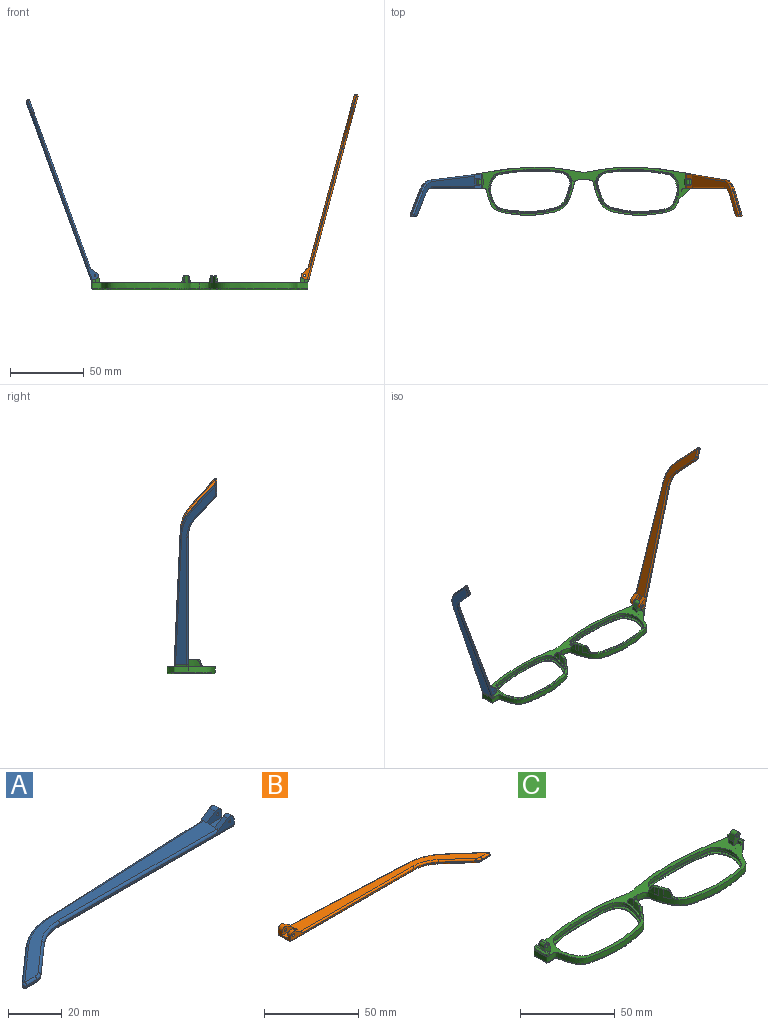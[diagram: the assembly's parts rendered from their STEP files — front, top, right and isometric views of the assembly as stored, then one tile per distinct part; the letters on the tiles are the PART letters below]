
ASSEMBLY  parts=3 mates=2
PART A: 43 faces, bbox 130.2x29.5x5.9 mm
  f0: plane 9.62x3.72mm, normal (1,0,0), area 24.7mm2, adj f1,f3,f4,f5,f10,f16,f18,f28
  f1: cylinder r=2.2mm len=3.45mm, axis (0,-1,0), area 11mm2, adj f0,f2,f4,f37
  f2: plane 6.01x3.91mm, normal (-0.55,0,0.84), area 12.7mm2, adj f1,f4,f9,f19,f37
  f3: plane 2.26x0.1mm, normal (0,0,1), area 0.1mm2, adj f0,f5,f18
  f4: plane 92.1x4.9mm, normal (0,-1,0), area 79.9mm2, adj f0,f1,f2,f14,f19,f36,f42
  f5: plane 93.42x4.13mm, normal (-0.04,1,0), area 64.8mm2, adj f0,f3,f11,f15,f17,f27,f28
  f6: plane 17.82x15.72mm, normal (-0.66,0.75,0), area 14.3mm2, adj f11,f12,f25,f30
  f7: plane 5.46x0.6mm, normal (0,-1,0), area 3.3mm2, adj f12,f13,f23,f32
  f8: plane 14.99x13.23mm, normal (0.66,-0.75,0), area 12mm2, adj f13,f14,f21,f34
  f9: plane 121.18x26.73mm, normal (0,0,1), area 627.7mm2, adj f2,f17,f19,f20,f21,f22,f23,f25
  f10: plane 129.1x27.08mm, normal (0,0,-1), area 686.5mm2, adj f0,f28,f29,f30,f32,f33,f34,f35
  f11: cylinder r=30mm len=18.52mm, axis (0,0,-1), area 12.2mm2, adj f5,f6,f26,f29
  f12: cylinder r=1mm len=1.75mm, axis (0,0,-1), area 1.5mm2, adj f6,f7,f24,f31
  f13: cylinder r=5mm len=3.31mm, axis (0,0,-1), area 2.2mm2, adj f7,f8,f22,f33
  f14: cylinder r=20mm len=13.23mm, axis (0,0,1), area 8.7mm2, adj f4,f8,f20,f35
  f15: plane 5.66x0.25mm, normal (0,0,-1), area 0.7mm2, adj f5,f17,f18
  f16: cylinder r=2.2mm len=3.45mm, axis (0,-1,0), area 14.8mm2, adj f0,f17,f18,f38
  f17: plane 6.01x3.91mm, normal (-0.55,0,0.84), area 16.9mm2, adj f5,f9,f15,f16,f18,f27,f38
  f18: plane 7.92x3.3mm, normal (0,1,0), area 15.9mm2, adj f0,f3,f15,f16,f17,f41
  f19: cylinder r=1mm len=84.18mm, axis (-1,0,0), area 131.4mm2, adj f2,f4,f9,f20
  f20: torus R=21mm, axis (0,0,1), area 23.1mm2, adj f9,f14,f19,f21
  f21: cylinder r=1mm len=15.65mm, axis (-0.75,-0.66,0), area 31.4mm2, adj f8,f9,f20,f22
  f22: torus R=4mm, axis (0,0,1), area 5.3mm2, adj f9,f13,f21,f23
  f23: cylinder r=1mm len=5.46mm, axis (-1,0,0), area 8.6mm2, adj f7,f9,f22,f24
  f24: sphere r=1mm, area 2.4mm2, adj f12,f23,f25
  f25: cylinder r=1mm len=18.48mm, axis (0.75,0.66,0), area 37.3mm2, adj f6,f9,f24,f26
  f26: torus R=29mm, axis (0,0,1), area 31.6mm2, adj f9,f11,f25,f27
  f27: cylinder r=1mm len=85.5mm, axis (1,0.04,0), area 133.5mm2, adj f5,f9,f17,f26
  f28: cylinder r=1mm len=93.46mm, axis (-1,-0.04,0), area 146.9mm2, adj f0,f5,f10,f29
  f29: torus R=29mm, axis (0,0,1), area 31.6mm2, adj f10,f11,f28,f30
  f30: cylinder r=1mm len=18.48mm, axis (-0.75,-0.66,0), area 37.3mm2, adj f6,f10,f29,f31
  f31: sphere r=1mm, area 2.4mm2, adj f12,f30,f32
  f32: cylinder r=1mm len=5.46mm, axis (1,0,0), area 8.6mm2, adj f7,f10,f31,f33
  f33: torus R=4mm, axis (0,0,1), area 5.3mm2, adj f10,f13,f32,f34
  f34: cylinder r=1mm len=15.65mm, axis (0.75,0.66,0), area 31.4mm2, adj f8,f10,f33,f35
  f35: torus R=21mm, axis (0,0,1), area 23.1mm2, adj f10,f14,f34,f36
  f36: cylinder r=1mm len=92.1mm, axis (1,0,0), area 144.7mm2, adj f0,f4,f10,f35
  f37: plane 7.92x4.7mm, normal (0,1,0), area 27mm2, adj f0,f1,f2,f39,f40,f42
  f38: plane 7.92x4.7mm, normal (0,-1,0), area 27mm2, adj f0,f16,f17,f39,f40,f41
  f39: plane 7.92x4.1mm, normal (0,0,1), area 32.5mm2, adj f0,f37,f38,f40
  f40: plane 4.1x1.4mm, normal (1,0,0), area 5.7mm2, adj f9,f37,f38,f39
  f41: cylinder r=0.5mm len=3.1mm, axis (0,-1,0), area 9.7mm2, adj f18,f38
  f42: cylinder r=0.5mm len=2.3mm, axis (0,-1,0), area 7.2mm2, adj f4,f37
PART B: 43 faces, bbox 130.2x29.5x5.9 mm
  f0: plane 9.62x3.72mm, normal (-1,0,0), area 24.7mm2, adj f1,f3,f4,f5,f10,f16,f18,f28
  f1: cylinder r=2.2mm len=3.45mm, axis (0,-1,0), area 11mm2, adj f0,f2,f4,f37
  f2: plane 6.01x3.91mm, normal (0.55,0,0.84), area 12.7mm2, adj f1,f4,f9,f19,f37
  f3: plane 2.26x0.1mm, normal (0,0,1), area 0.1mm2, adj f0,f5,f18
  f4: plane 92.1x4.9mm, normal (0,-1,0), area 78.2mm2, adj f0,f1,f2,f14,f19,f36,f42
  f5: plane 93.42x4.13mm, normal (0.04,1,0), area 64.8mm2, adj f0,f3,f11,f15,f17,f27,f28
  f6: plane 17.82x15.72mm, normal (0.66,0.75,0), area 14.3mm2, adj f11,f12,f25,f30
  f7: plane 5.46x0.6mm, normal (0,-1,0), area 3.3mm2, adj f12,f13,f23,f32
  f8: plane 14.99x13.23mm, normal (-0.66,-0.75,0), area 12mm2, adj f13,f14,f21,f34
  f9: plane 121.18x26.73mm, normal (0,0,1), area 627.7mm2, adj f2,f17,f19,f20,f21,f22,f23,f25
  f10: plane 129.1x27.08mm, normal (0,0,-1), area 686.5mm2, adj f0,f28,f29,f30,f32,f33,f34,f35
  f11: cylinder r=30mm len=18.52mm, axis (0,0,-1), area 12.2mm2, adj f5,f6,f26,f29
  f12: cylinder r=1mm len=1.75mm, axis (0,0,-1), area 1.5mm2, adj f6,f7,f24,f31
  f13: cylinder r=5mm len=3.31mm, axis (0,0,-1), area 2.2mm2, adj f7,f8,f22,f33
  f14: cylinder r=20mm len=13.23mm, axis (0,0,1), area 8.7mm2, adj f4,f8,f20,f35
  f15: plane 5.66x0.25mm, normal (0,0,-1), area 0.7mm2, adj f5,f17,f18
  f16: cylinder r=2.2mm len=3.45mm, axis (0,-1,0), area 14.8mm2, adj f0,f17,f18,f38
  f17: plane 6.01x3.91mm, normal (0.55,0,0.84), area 16.9mm2, adj f5,f9,f15,f16,f18,f27,f38
  f18: plane 7.92x3.3mm, normal (0,1,0), area 14.3mm2, adj f0,f3,f15,f16,f17,f41
  f19: cylinder r=1mm len=84.18mm, axis (1,0,0), area 131.4mm2, adj f2,f4,f9,f20
  f20: torus R=21mm, axis (0,0,1), area 23.1mm2, adj f9,f14,f19,f21
  f21: cylinder r=1mm len=15.65mm, axis (0.75,-0.66,0), area 31.4mm2, adj f8,f9,f20,f22
  f22: torus R=4mm, axis (0,0,1), area 5.3mm2, adj f9,f13,f21,f23
  f23: cylinder r=1mm len=5.46mm, axis (1,0,0), area 8.6mm2, adj f7,f9,f22,f24
  f24: sphere r=1mm, area 2.4mm2, adj f12,f23,f25
  f25: cylinder r=1mm len=18.48mm, axis (-0.75,0.66,0), area 37.3mm2, adj f6,f9,f24,f26
  f26: torus R=29mm, axis (0,0,1), area 31.6mm2, adj f9,f11,f25,f27
  f27: cylinder r=1mm len=85.5mm, axis (-1,0.04,0), area 133.5mm2, adj f5,f9,f17,f26
  f28: cylinder r=1mm len=93.46mm, axis (1,-0.04,0), area 146.9mm2, adj f0,f5,f10,f29
  f29: torus R=29mm, axis (0,0,1), area 31.6mm2, adj f10,f11,f28,f30
  f30: cylinder r=1mm len=18.48mm, axis (0.75,-0.66,0), area 37.3mm2, adj f6,f10,f29,f31
  f31: sphere r=1mm, area 2.4mm2, adj f12,f30,f32
  f32: cylinder r=1mm len=5.46mm, axis (-1,0,0), area 8.6mm2, adj f7,f10,f31,f33
  f33: torus R=4mm, axis (0,0,1), area 5.3mm2, adj f10,f13,f32,f34
  f34: cylinder r=1mm len=15.65mm, axis (-0.75,0.66,0), area 31.4mm2, adj f8,f10,f33,f35
  f35: torus R=21mm, axis (0,0,1), area 23.1mm2, adj f10,f14,f34,f36
  f36: cylinder r=1mm len=92.1mm, axis (-1,0,0), area 144.7mm2, adj f0,f4,f10,f35
  f37: plane 7.92x4.7mm, normal (0,1,0), area 25.4mm2, adj f0,f1,f2,f39,f40,f42
  f38: plane 7.92x4.7mm, normal (0,-1,0), area 25.4mm2, adj f0,f16,f17,f39,f40,f41
  f39: plane 7.92x4.1mm, normal (0,0,1), area 32.5mm2, adj f0,f37,f38,f40
  f40: plane 4.1x1.4mm, normal (-1,0,0), area 5.7mm2, adj f9,f37,f38,f39
  f41: cylinder r=0.88mm len=3.1mm, axis (0,-1,0), area 17mm2, adj f18,f38
  f42: cylinder r=0.88mm len=2.3mm, axis (0,-1,0), area 12.6mm2, adj f4,f37
PART C: 88 faces, bbox 148.2x33.5x17.9 mm
  f0: extruded ~10.56x5mm, area 41.6mm2, adj f2,f37,f38,f40,f43
  f1: extruded ~5.01x5mm, area 12.8mm2, adj f2,f37,f39
  f2: plane 147.77x33.33mm, normal (0,0,1), area 824.9mm2, adj f0,f1,f4,f5,f6,f7,f8,f21
  f3: plane 3.96x1.78mm, normal (0,0,1), area 0mm2, adj f7,f36
  f4: plane 1.2x0.04mm, normal (0,0,1), area 0mm2, adj f2,f7,f22
  f5: plane 6.91x4.89mm, normal (0,1,0), area 21mm2, adj f2,f21,f25,f27,f28,f29,f30,f31
  f6: plane 6.91x4.89mm, normal (0,-1,0), area 21mm2, adj f2,f21,f26,f27,f28,f29,f30,f31
  f7: extruded ~73.32x32.67mm, area 509.4mm2, adj f2,f3,f4,f8,f13,f14,f15,f16
  f8: extruded ~33.86x3.5mm, area 119.4mm2, adj f2,f7,f19,f52
  f9: plane 144.79x30.69mm, normal (0,0,-1), area 451.5mm2, adj f14,f16,f18,f19,f20,f57,f59,f61
  f10: plane 56.61x30.2mm, normal (0,0,1), area 187.1mm2, adj f11,f20
  f11: extruded ~56.31x30.04mm, area 148mm2, adj f10,f12
  f12: extruded ~56.31x30.04mm, area 296.1mm2, adj f11,f41,f42
  f13: plane 2.59x0.69mm, normal (0,0,1), area 0mm2, adj f7,f35
  f14: bspline ~73.03x25.58mm, area 149.9mm2, adj f7,f9,f15,f57
  f15: bspline ~1x1mm, area 0.8mm2, adj f7,f14,f16
  f16: bspline ~8.66x1.21mm, area 12.7mm2, adj f7,f9,f15,f17
  f17: bspline ~1.04x1mm, area 0.8mm2, adj f7,f16,f18
  f18: bspline ~45.4x5.77mm, area 61.6mm2, adj f7,f9,f17,f19
  f19: bspline ~36.19x4.34mm, area 53.5mm2, adj f8,f9,f18,f62
  f20: bspline ~55.75x29.24mm, area 220mm2, adj f9,f10
  f21: plane 3.8x2.3mm, normal (-1,0,0), area 8.7mm2, adj f2,f5,f6,f28
  f22: plane 2.79x2.56mm, normal (0,-1,0), area 3.9mm2, adj f4,f26,f27,f33,f44
  f23: plane 7.68x1.6mm, normal (0.94,0,-0.34), area 13.1mm2, adj f2,f33,f34,f44
  f24: plane 2.1x1.69mm, normal (0,1,0), area 2.8mm2, adj f2,f25,f27,f34,f44
  f25: plane 3.41x2.1mm, normal (-1,0,0), area 7.2mm2, adj f2,f5,f24,f27
  f26: plane 2.46x2.1mm, normal (-1,0,0), area 5.2mm2, adj f2,f6,f22,f27
  f27: plane 9.67x1.25mm, normal (0,0,1), area 8.8mm2, adj f5,f6,f22,f24,f25,f26,f29,f44
  f28: plane 3.8x3.31mm, normal (-0.94,0,0.34), area 13.4mm2, adj f5,f6,f21,f31
  f29: plane 3.8x2.21mm, normal (0.94,0,-0.34), area 8.9mm2, adj f5,f6,f27,f30
  f30: cylinder r=1.98mm len=3.8mm, axis (0,-1,0), area 11.5mm2, adj f5,f6,f29,f31
  f31: cylinder r=1.98mm len=3.8mm, axis (0,1,0), area 11.5mm2, adj f5,f6,f28,f30
  f32: cylinder r=0.95mm len=3.8mm, axis (0,-1,0), area 22.7mm2, adj f5,f6
  f33: cone r=1mm half-angle=20deg, axis (0,0,1), area 2.3mm2, adj f2,f22,f23,f44
  f34: cylinder r=1mm len=2.28mm, axis (-0.34,0,-0.94), area 3mm2, adj f2,f23,f24,f44
  f35: extruded ~5x2.58mm, area 12.9mm2, adj f7,f13,f38,f39
  f36: extruded ~5x3.93mm, area 20.5mm2, adj f3,f7,f38,f40,f43
  f37: extruded ~5x0.31mm, area 1.6mm2, adj f0,f1,f2,f38
  f38: plane 7.62x2.87mm, normal (0,0,1), area 8.6mm2, adj f0,f7,f35,f36,f37,f39,f40
  f39: bspline ~15.49x15.48mm, area 16.3mm2, adj f1,f2,f7,f35,f38
  f40: bspline ~7.28x7.28mm, area 5.6mm2, adj f0,f36,f38,f43
  f41: plane 56.54x30.13mm, normal (0,0,-1), area 51.5mm2, adj f12,f42
  f42: bspline ~55.69x29.23mm, area 101.4mm2, adj f2,f12,f41
  f43: bspline ~3.67x3.45mm, area 5.2mm2, adj f0,f2,f7,f36,f40
  f44: plane 9.73x1.44mm, normal (0.34,0,0.94), area 13.9mm2, adj f22,f23,f24,f27,f33,f34
  f45: extruded ~10.56x5mm, area 41.6mm2, adj f2,f80,f81,f83,f86
  f46: extruded ~5.01x5mm, area 12.8mm2, adj f2,f80,f82
  f47: plane 3.96x1.78mm, normal (0,0,1), area 0mm2, adj f51,f79
  f48: plane 1.2x0.04mm, normal (0,0,1), area 0mm2, adj f2,f51,f65
  f49: plane 6.91x4.89mm, normal (0,1,0), area 21mm2, adj f2,f64,f68,f70,f71,f72,f73,f74
  f50: plane 6.91x4.89mm, normal (0,-1,0), area 21mm2, adj f2,f64,f69,f70,f71,f72,f73,f74
  f51: extruded ~73.32x32.67mm, area 509.4mm2, adj f2,f7,f47,f48,f52,f56,f57,f58
  f52: extruded ~33.86x3.5mm, area 119.4mm2, adj f2,f8,f51,f62
  f53: plane 56.61x30.2mm, normal (0,0,1), area 187.1mm2, adj f54,f63
  f54: extruded ~56.31x30.04mm, area 148mm2, adj f53,f55
  f55: extruded ~56.31x30.04mm, area 296.1mm2, adj f54,f84,f85
  f56: plane 2.59x0.69mm, normal (0,0,1), area 0mm2, adj f51,f78
  f57: bspline ~73.03x25.58mm, area 150mm2, adj f9,f14,f51,f58
  f58: bspline ~1x1mm, area 0.8mm2, adj f51,f57,f59
  f59: bspline ~8.66x1.21mm, area 12.7mm2, adj f9,f51,f58,f60
  f60: bspline ~1.04x1mm, area 0.7mm2, adj f51,f59,f61
  f61: bspline ~45.4x5.77mm, area 61.6mm2, adj f9,f51,f60,f62
  f62: bspline ~36.19x4.34mm, area 53.5mm2, adj f9,f19,f52,f61
  f63: bspline ~55.75x29.24mm, area 220mm2, adj f9,f53
  f64: plane 3.8x2.3mm, normal (1,0,0), area 8.7mm2, adj f2,f49,f50,f71
  f65: plane 2.79x2.56mm, normal (0,-1,0), area 3.9mm2, adj f48,f69,f70,f76,f87
  f66: plane 7.68x1.6mm, normal (-0.94,0,-0.34), area 13.1mm2, adj f2,f76,f77,f87
  f67: plane 2.1x1.69mm, normal (0,1,0), area 2.8mm2, adj f2,f68,f70,f77,f87
  f68: plane 3.41x2.1mm, normal (1,0,0), area 7.2mm2, adj f2,f49,f67,f70
  f69: plane 2.46x2.1mm, normal (1,0,0), area 5.2mm2, adj f2,f50,f65,f70
  f70: plane 9.67x1.25mm, normal (0,0,1), area 8.8mm2, adj f49,f50,f65,f67,f68,f69,f72,f87
  f71: plane 3.8x3.31mm, normal (0.94,0,0.34), area 13.4mm2, adj f49,f50,f64,f74
  f72: plane 3.8x2.21mm, normal (-0.94,0,-0.34), area 8.9mm2, adj f49,f50,f70,f73
  f73: cylinder r=1.98mm len=3.8mm, axis (0,-1,0), area 11.5mm2, adj f49,f50,f72,f74
  f74: cylinder r=1.98mm len=3.8mm, axis (0,1,0), area 11.5mm2, adj f49,f50,f71,f73
  f75: cylinder r=0.95mm len=3.8mm, axis (0,-1,0), area 22.7mm2, adj f49,f50
  f76: cone r=1mm half-angle=20deg, axis (0,0,1), area 2.3mm2, adj f2,f65,f66,f87
  f77: cylinder r=1mm len=2.28mm, axis (0.34,0,-0.94), area 3mm2, adj f2,f66,f67,f87
  f78: extruded ~5x2.58mm, area 12.9mm2, adj f51,f56,f81,f82
  f79: extruded ~5x3.93mm, area 20.5mm2, adj f47,f51,f81,f83,f86
  f80: extruded ~5x0.31mm, area 1.6mm2, adj f2,f45,f46,f81
  f81: plane 7.62x2.87mm, normal (0,0,1), area 8.6mm2, adj f45,f51,f78,f79,f80,f82,f83
  f82: bspline ~15.49x15.48mm, area 16.3mm2, adj f2,f46,f51,f78,f81
  f83: bspline ~7.28x7.28mm, area 5.6mm2, adj f45,f79,f81,f86
  f84: plane 56.54x30.13mm, normal (0,0,-1), area 51.5mm2, adj f55,f85
  f85: bspline ~55.69x29.23mm, area 101.4mm2, adj f2,f55,f84
  f86: bspline ~3.67x3.45mm, area 5.2mm2, adj f2,f45,f51,f79,f83
  f87: plane 9.73x1.44mm, normal (-0.34,0,0.94), area 13.9mm2, adj f65,f66,f67,f70,f76,f77
PLACE A rot(axis=(0,1,0),70deg) t=(-164.62,-11.41,86.54)mm
PLACE B rot(axis=(0,-1,0),75deg) t=(-11.67,-11.41,-31.01)mm
PLACE C t=(-69.62,-6.9,23.33)mm
MATE revolute A.f1 <-> C.f74  axis (0,-1,0) through (-140.74,-2.95,31.75)mm
MATE revolute B.f41 <-> C.f30  axis (0,-1,0) through (1.34,-2.95,31.81)mm
